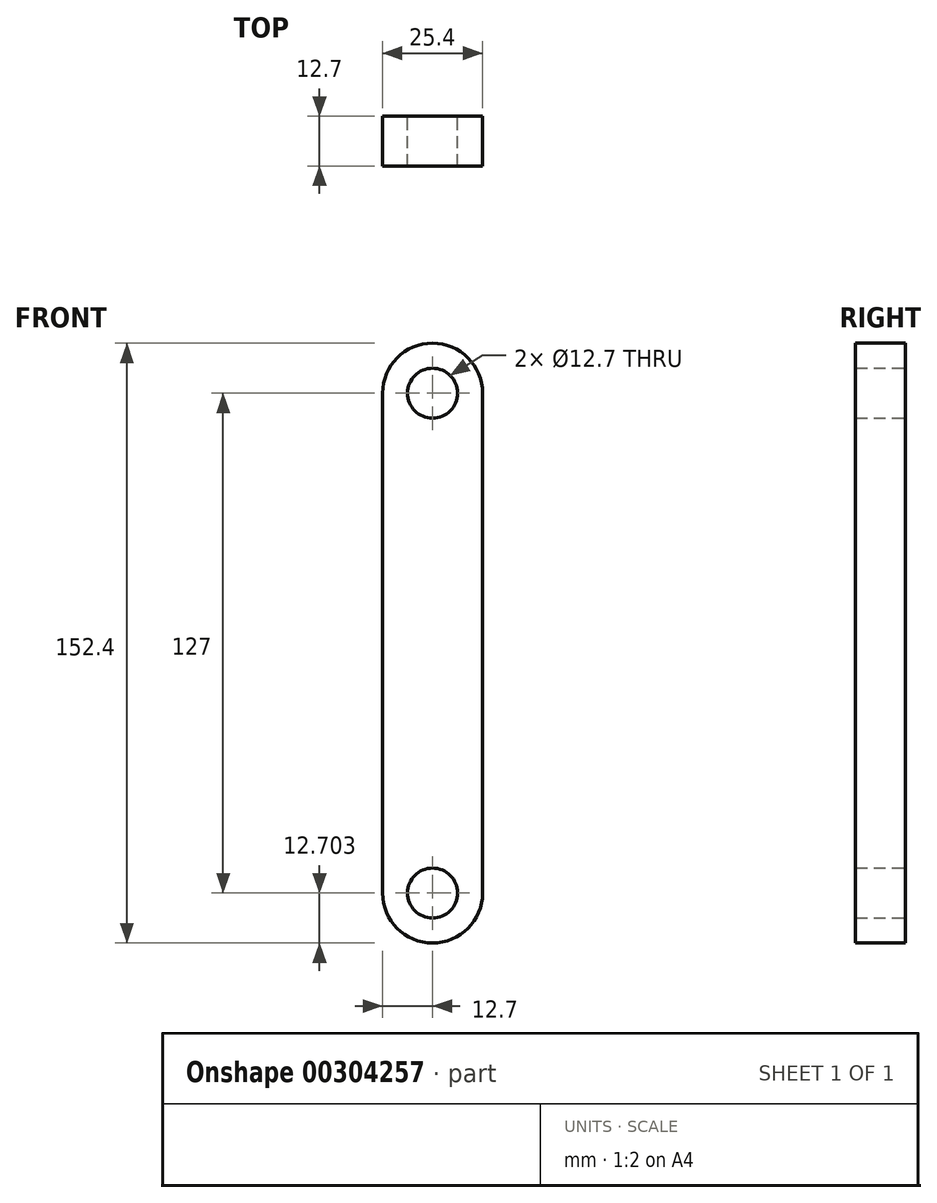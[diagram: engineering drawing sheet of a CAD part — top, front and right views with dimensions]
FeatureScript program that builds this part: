
annotation { "Feature Type Name" : "Feature", "Feature Type Description" : "" }
export const myFeature = defineFeature(function(context is Context, id is Id, definition is map)
    precondition{}
    {
        {
            var Q0;
            Q0=qCreatedBy(makeId("Front.planeOp"),FACE);
            var sketch = newSketch(context, id + "F0", { "sketchPlane" : qUnion([Q0])});
            skCircle(sketch, "E0", {"center": v(0, 114.56) * mm, "radius": 12.7 * mm});
            skCircle(sketch, "E1", {"center": v(0, -12.44) * mm, "radius": 12.7 * mm});
            skLineSegment(sketch, "E2", {"start": v(12.7, 114.56) * mm, "end": v(12.7, -12.44) * mm});
            skCircle(sketch, "E3", {"center": v(0, 114.56) * mm, "radius": 6.35 * mm});
            skCircle(sketch, "E4", {"center": v(0, -12.44) * mm, "radius": 6.35 * mm});
            skLineSegment(sketch, "E5", {"start": v(-12.7, -12.44) * mm, "end": v(-12.7, 114.56) * mm});
            skSolve(sketch);
        }
        {
            var Q0;
            Q0=qSketchRegion(id+"F0",true);
            extrude(context, id + "F1", {"entities" : qUnion([Q0]), "endBound" : BoundingType.SYMMETRIC, "depth" : 12.7 * mm});
        }
    });
